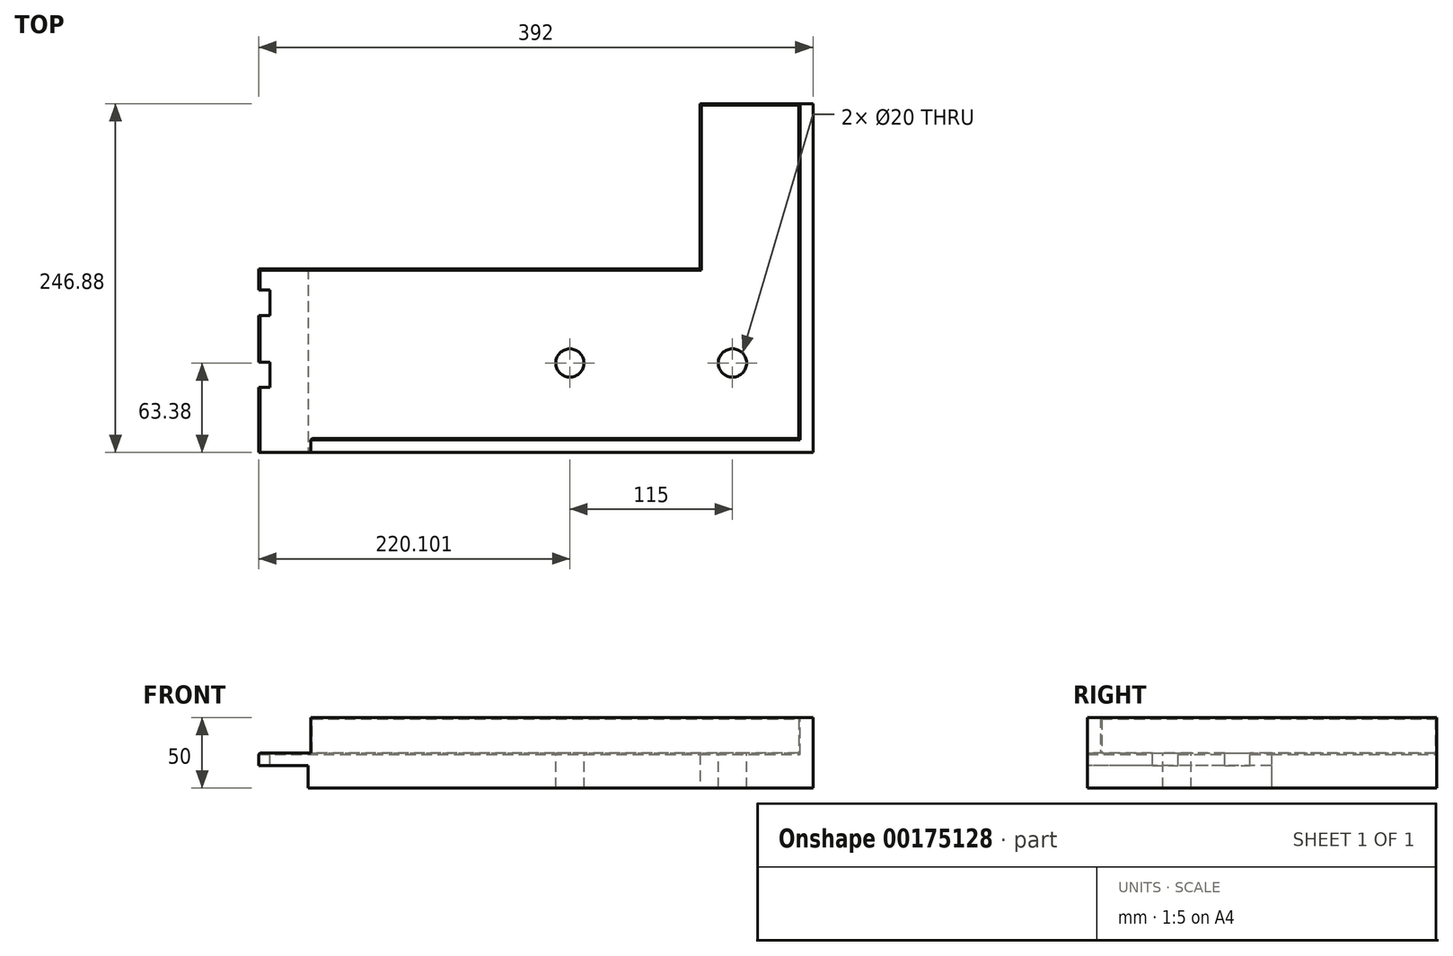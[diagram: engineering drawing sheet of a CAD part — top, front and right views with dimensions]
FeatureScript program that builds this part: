
annotation { "Feature Type Name" : "Feature", "Feature Type Description" : "" }
export const myFeature = defineFeature(function(context is Context, id is Id, definition is map)
    precondition{}
    {
        {
            var Q0;
            Q0=qCreatedBy(makeId("Top.planeOp"),FACE);
            var sketch = newSketch(context, id + "F0", { "sketchPlane" : qUnion([Q0])});
            skLineSegment(sketch, "E0", {"start": v(0, 0) * mm, "end": v(0, 246.88) * mm});
            skLineSegment(sketch, "E1", {"start": v(0, 246.88) * mm, "end": v(-80, 246.88) * mm});
            skLineSegment(sketch, "E2", {"start": v(-80, 246.88) * mm, "end": v(-80, 130) * mm});
            skLineSegment(sketch, "E3", {"start": v(-80, 130) * mm, "end": v(-392, 130) * mm});
            skLineSegment(sketch, "E4", {"start": v(-392, 130) * mm, "end": v(-392, 0) * mm});
            skLineSegment(sketch, "E5", {"start": v(-392, 0) * mm, "end": v(0, 0) * mm});
            skSolve(sketch);
        }
        {
            var Q0;
            Q0=makeQuery(id+"F0.imprint","IMPRINT",FACE,{"disambiguationData":[TD([[makeQuery(id+"F0.imprint","IMPRINT",EDGE,{"derivedFrom":sQuery(id+"F0.wireOp",EDGE,"E0")}),1.0]])]});
            extrude(context, id + "F1", {"entities" : qUnion([Q0]), "depth" : 25 * mm});
        }
        {
            var Q0;
            Q0=makeQuery(id+"F1.opExtrude","CAP_FACE",FACE,{"disambiguationData":[OSD([sQuery(id+"F0.wireOp",EDGE,"E0"),sQuery(id+"F0.wireOp",EDGE,"E1"),sQuery(id+"F0.wireOp",EDGE,"E2"),sQuery(id+"F0.wireOp",EDGE,"E3"),sQuery(id+"F0.wireOp",EDGE,"E4"),sQuery(id+"F0.wireOp",EDGE,"E5")])],"isStart":false});
            var sketch = newSketch(context, id + "F2", { "sketchPlane" : qUnion([Q0])});
            skLineSegment(sketch, "E6", {"start": v(-392, 0) * mm, "end": v(-392, 46) * mm});
            skLineSegment(sketch, "E7", {"start": v(-392, 46) * mm, "end": v(-384, 46) * mm});
            skLineSegment(sketch, "E8", {"start": v(-384, 46) * mm, "end": v(-384, 64) * mm});
            skLineSegment(sketch, "E9", {"start": v(-384, 64) * mm, "end": v(-392, 64) * mm});
            skLineSegment(sketch, "E10", {"start": v(-392, 64) * mm, "end": v(-392, 97) * mm});
            skLineSegment(sketch, "E11", {"start": v(-392, 97) * mm, "end": v(-384, 97) * mm});
            skLineSegment(sketch, "E12", {"start": v(-384, 97) * mm, "end": v(-384, 115) * mm});
            skLineSegment(sketch, "E13", {"start": v(-384, 115) * mm, "end": v(-392, 115) * mm});
            skSolve(sketch);
        }
        {
            var Q0;
            {var subQ0=sQuery(id+"F2.wireOp",EDGE,"E11");Q0=makeQuery(id+"F2.imprint","IMPRINT",FACE,{"disambiguationData":[TD([[makeQuery(id+"F2.imprint","IMPRINT",EDGE,{"derivedFrom":subQ0}),1.0]])]});}
            var Q1;
            {var subQ0=sQuery(id+"F2.wireOp",EDGE,"E7");Q1=makeQuery(id+"F2.imprint","IMPRINT",FACE,{"disambiguationData":[TD([[makeQuery(id+"F2.imprint","IMPRINT",EDGE,{"derivedFrom":subQ0}),1.0]])]});}
            extrude(context, id + "F3", {"entities" : qUnion([Q0, Q1]), "operationType" : NewBodyOperationType.REMOVE, "endBound" : BoundingType.THROUGH_ALL, "oppositeDirection" : true, "depth" : 25.4 * mm});
        }
        {
            var Q0;
            Q0=makeQuery(id+"F1.opExtrude","SWEPT_FACE",FACE,{"disambiguationData":[OSD([sQuery(id+"F0.wireOp",EDGE,"E5")])]});
            var sketch = newSketch(context, id + "F4", { "sketchPlane" : qUnion([Q0])});
            skLineSegment(sketch, "E14", {"start": v(-392, 0) * mm, "end": v(-392, 16) * mm});
            skLineSegment(sketch, "E15", {"start": v(-392, 16) * mm, "end": v(-357, 16) * mm});
            skLineSegment(sketch, "E16", {"start": v(-357, 16) * mm, "end": v(-357, 0) * mm});
            skSolve(sketch);
        }
        {
            var Q0;
            {var subQ0=sQuery(id+"F4.wireOp",EDGE,"E14");Q0=makeQuery(id+"F4.imprint","IMPRINT",FACE,{"disambiguationData":[TD([[makeQuery(id+"F4.imprint","IMPRINT",EDGE,{"derivedFrom":subQ0}),1.0]])]});}
            extrude(context, id + "F5", {"entities" : qUnion([Q0]), "operationType" : NewBodyOperationType.REMOVE, "endBound" : BoundingType.THROUGH_ALL, "oppositeDirection" : true, "depth" : 25.4 * mm});
        }
        {
            var Q0;
            Q0=makeQuery(id+"F1.opExtrude","CAP_FACE",FACE,{"disambiguationData":[OSD([sQuery(id+"F0.wireOp",EDGE,"E0"),sQuery(id+"F0.wireOp",EDGE,"E1"),sQuery(id+"F0.wireOp",EDGE,"E2"),sQuery(id+"F0.wireOp",EDGE,"E3"),sQuery(id+"F0.wireOp",EDGE,"E4"),sQuery(id+"F0.wireOp",EDGE,"E5")])],"isStart":false});
            var sketch = newSketch(context, id + "F6", { "sketchPlane" : qUnion([Q0])});
            skLineSegment(sketch, "E17", {"start": v(-355.14, 0) * mm, "end": v(-355.14, 10) * mm});
            skLineSegment(sketch, "E18", {"start": v(-355.14, 10) * mm, "end": v(-10, 10) * mm});
            skLineSegment(sketch, "E19", {"start": v(-10, 10) * mm, "end": v(-10, 246.88) * mm});
            skLineSegment(sketch, "E20", {"start": v(-10, 246.88) * mm, "end": v(0, 246.88) * mm});
            skLineSegment(sketch, "E21", {"start": v(-355.14, 0) * mm, "end": v(0, 0) * mm});
            skLineSegment(sketch, "E22", {"start": v(0, 0) * mm, "end": v(0, 246.88) * mm});
            skSolve(sketch);
        }
        {
            var Q0;
            Q0=makeQuery(id+"F6.imprint","IMPRINT",FACE,{"disambiguationData":[TD([[makeQuery(id+"F6.imprint","IMPRINT",EDGE,{"derivedFrom":sQuery(id+"F6.wireOp",EDGE,"E17")}),-1.0]])]});
            extrude(context, id + "F7", {"entities" : qUnion([Q0]), "operationType" : NewBodyOperationType.ADD, "depth" : 25 * mm});
        }
        {
            var Q0;
            {var subQ0=sQuery(id+"F0.wireOp",EDGE,"E5");var subQ1=sQuery(id+"F0.wireOp",EDGE,"E4");Q0=makeQuery(id+"F3.boolean.opBoolean","SPLIT",EDGE,{"disambiguationData":[TD([makeQuery(id+"F1.opExtrude","SWEPT_FACE",FACE,{"disambiguationData":[OSD([subQ0])]})])],"derivedFrom":makeQuery(id+"F1.opExtrude","CAP_EDGE",EDGE,{"disambiguationData":[OSD([subQ1])],"isStart":false})});}
            var Q1;
            Q1=makeQuery(id+"F3.boolean.opBoolean","COPY",EDGE,{"derivedFrom":makeQuery(id+"F3.opExtrude","CAP_EDGE",EDGE,{"disambiguationData":[OSD([sQuery(id+"F2.wireOp",EDGE,"E8")])],"isStart":true})});
            var Q2;
            {var subQ0=sQuery(id+"F0.wireOp",EDGE,"E4");Q2=makeQuery(id+"F3.boolean.opBoolean","SPLIT",EDGE,{"disambiguationData":[TD([makeQuery(id+"F3.opExtrude","SWEPT_FACE",FACE,{"disambiguationData":[OSD([sQuery(id+"F2.wireOp",EDGE,"E9")])]})])],"derivedFrom":makeQuery(id+"F1.opExtrude","CAP_EDGE",EDGE,{"disambiguationData":[OSD([subQ0])],"isStart":false})});}
            var Q3;
            Q3=makeQuery(id+"F3.boolean.opBoolean","COPY",EDGE,{"derivedFrom":makeQuery(id+"F3.opExtrude","CAP_EDGE",EDGE,{"disambiguationData":[OSD([sQuery(id+"F2.wireOp",EDGE,"E12")])],"isStart":true})});
            var Q4;
            {var subQ0=sQuery(id+"F0.wireOp",EDGE,"E4");var subQ1=sQuery(id+"F0.wireOp",EDGE,"E3");Q4=makeQuery(id+"F3.boolean.opBoolean","SPLIT",EDGE,{"disambiguationData":[TD([makeQuery(id+"F1.opExtrude","SWEPT_FACE",FACE,{"disambiguationData":[OSD([subQ1])]})])],"derivedFrom":makeQuery(id+"F1.opExtrude","CAP_EDGE",EDGE,{"disambiguationData":[OSD([subQ0])],"isStart":false})});}
            var Q5;
            Q5=makeQuery(id+"F3.boolean.opBoolean","COPY",EDGE,{"derivedFrom":makeQuery(id+"F3.opExtrude","CAP_EDGE",EDGE,{"disambiguationData":[OSD([sQuery(id+"F2.wireOp",EDGE,"E9")])],"isStart":true})});
            var Q6;
            Q6=makeQuery(id+"F3.boolean.opBoolean","COPY",EDGE,{"derivedFrom":makeQuery(id+"F3.opExtrude","CAP_EDGE",EDGE,{"disambiguationData":[OSD([sQuery(id+"F2.wireOp",EDGE,"E7")])],"isStart":true})});
            var Q7;
            Q7=makeQuery(id+"F3.boolean.opBoolean","COPY",EDGE,{"derivedFrom":makeQuery(id+"F3.opExtrude","CAP_EDGE",EDGE,{"disambiguationData":[OSD([sQuery(id+"F2.wireOp",EDGE,"E13")])],"isStart":true})});
            var Q8;
            Q8=makeQuery(id+"F3.boolean.opBoolean","COPY",EDGE,{"derivedFrom":makeQuery(id+"F3.opExtrude","CAP_EDGE",EDGE,{"disambiguationData":[OSD([sQuery(id+"F2.wireOp",EDGE,"E11")])],"isStart":true})});
            chamfer(context, id + "F8", {"entities" : qUnion([Q0, Q1, Q2, Q3, Q4, Q5, Q6, Q7, Q8]), "width" : 1 * mm, "tangentPropagation" : true});
        }
        {
            var Q0;
            Q0=makeQuery(id+"F1.opExtrude","CAP_EDGE",EDGE,{"disambiguationData":[OSD([sQuery(id+"F0.wireOp",EDGE,"E3")])],"isStart":false});
            var Q1;
            Q1=makeQuery(id+"F1.opExtrude","CAP_EDGE",EDGE,{"disambiguationData":[OSD([sQuery(id+"F0.wireOp",EDGE,"E2")])],"isStart":false});
            chamfer(context, id + "F9", {"entities" : qUnion([Q0, Q1]), "width" : 1 * mm, "tangentPropagation" : true});
        }
        {
            var Q0;
            Q0=makeQuery(id+"F7.opExtrude","CAP_EDGE",EDGE,{"disambiguationData":[OSD([sQuery(id+"F6.wireOp",EDGE,"E18")])],"isStart":false});
            var Q1;
            Q1=makeQuery(id+"F7.opExtrude","CAP_EDGE",EDGE,{"disambiguationData":[OSD([sQuery(id+"F6.wireOp",EDGE,"E19")])],"isStart":false});
            chamfer(context, id + "F10", {"entities" : qUnion([Q0, Q1]), "width" : 1 * mm, "tangentPropagation" : true});
        }
        {
            var Q0;
            Q0=makeQuery(id+"F7.opExtrude","SWEPT_EDGE",EDGE,{"disambiguationData":[OSD([sQuery(id+"F6.wireOp",EDGE,"E17"),sQuery(id+"F6.wireOp",EDGE,"E18")])]});
            chamfer(context, id + "F11", {"entities" : qUnion([Q0]), "width" : 1 * mm, "tangentPropagation" : true});
        }
        {
            var Q0;
            Q0=makeQuery(id+"F1.opExtrude","CAP_EDGE",EDGE,{"disambiguationData":[OSD([sQuery(id+"F0.wireOp",EDGE,"E1")])],"isStart":false});
            var Q1;
            Q1=makeQuery(id+"F7.opExtrude","SWEPT_EDGE",EDGE,{"disambiguationData":[OSD([sQuery(id+"F0.wireOp",EDGE,"E1"),sQuery(id+"F6.wireOp",EDGE,"E19"),sQuery(id+"F6.wireOp",EDGE,"E20")])]});
            chamfer(context, id + "F12", {"entities" : qUnion([Q0, Q1]), "width" : 1 * mm, "tangentPropagation" : true});
        }
        {
            var Q0;
            Q0=makeQuery(id+"F1.opExtrude","CAP_FACE",FACE,{"disambiguationData":[OSD([sQuery(id+"F0.wireOp",EDGE,"E0"),sQuery(id+"F0.wireOp",EDGE,"E1"),sQuery(id+"F0.wireOp",EDGE,"E2"),sQuery(id+"F0.wireOp",EDGE,"E3"),sQuery(id+"F0.wireOp",EDGE,"E4"),sQuery(id+"F0.wireOp",EDGE,"E5")])],"isStart":false});
            var sketch = newSketch(context, id + "F13", { "sketchPlane" : qUnion([Q0])});
            skCircle(sketch, "E23", {"center": v(-171.9, 63.38) * mm, "radius": 10 * mm});
            skLineSegment(sketch, "E24", {"start": v(-171.9, 63.38) * mm, "end": v(-56.9, 63.38) * mm});
            skCircle(sketch, "E25", {"center": v(-56.9, 63.38) * mm, "radius": 10 * mm});
            skSolve(sketch);
        }
        {
            var Q0;
            Q0=makeQuery(id+"F13.imprint","IMPRINT",FACE,{"disambiguationData":[TD([[makeQuery(id+"F13.imprint","IMPRINT",EDGE,{"derivedFrom":sQuery(id+"F13.wireOp",EDGE,"E25")}),1.0]])]});
            var Q1;
            Q1=makeQuery(id+"F13.imprint","IMPRINT",FACE,{"disambiguationData":[TD([[makeQuery(id+"F13.imprint","IMPRINT",EDGE,{"derivedFrom":sQuery(id+"F13.wireOp",EDGE,"E23")}),1.0]])]});
            extrude(context, id + "F14", {"entities" : qUnion([Q0, Q1]), "operationType" : NewBodyOperationType.REMOVE, "endBound" : BoundingType.THROUGH_ALL, "oppositeDirection" : true, "depth" : 25.4 * mm});
        }
    });
